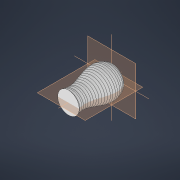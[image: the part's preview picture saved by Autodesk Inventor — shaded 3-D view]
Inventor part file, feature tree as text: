
AUTODESK INVENTOR PART (.ipt)
format: ipt  version: 2021 (Build 250183000, 183)  size: 1,588,224 bytes
history: native  units: mm
features: sketch x5, extrude x2, other x2, revolve x1, plane x1, sweep x1, helix x1
ambient origin geometry x8: Origin, YZ Plane, XZ Plane, XY Plane, X Axis, Y Axis, Z Axis, Center Point
bodies: Body1 (feature_tree), Body2 (feature_tree)
feature tree (13):
  revolve  "Revolution2"  Angle=90.0deg
  plane  "Work Plane1"
  sweep  "Sweep3"
  extrude  "Extrusion7"  Depth=80.0mm
  extrude  "Extrusion8"  Depth=20.0mm
  sketch  "Sketch1"  dims[d37=240.0mm d52=90.0deg]
  other  "Srf4"
  sketch  "3D Sketch3"
  sketch  "Sketch19"  dims[d71=40.0mm d73=240.0mm]
  sketch  "Sketch24"  dims[d74=150.0mm d75=80.0mm]
  sketch  "Sketch25"  dims[d76=60.0mm d78=120.0mm d79=20.0mm d80=-20.0mm d89=100.0mm d90=20.0mm d91=240.0mm d92=40.0mm d93=0.0mm d94=90.0deg d95=90.0deg d96=0.0mm d97=0.0mm d99=0.0mm d100=0.0mm d107=20.0mm d108=20.0mm d122=20.0mm d123=200.0mm d124=20.0mm d125=0.0mm d126=200.0mm d127=20.0mm d128=0.0mm d129=52.0mm d130=20.0mm d131=5.0mm d29=0.5mm d30=0.872665mm d31=0.5mm d32=0.872665mm d110=0.5mm d111=0.872665mm d112=0.5mm d113=0.872665mm]
  helix  "Coil3"  [1 undecoded]
  other  "3D Intersection3"
note: 1 required parameter value undecoded (feature->parameter linkage not recoverable at this tier; creation-order binding heuristic only, values carry confidence <= 0.55)
